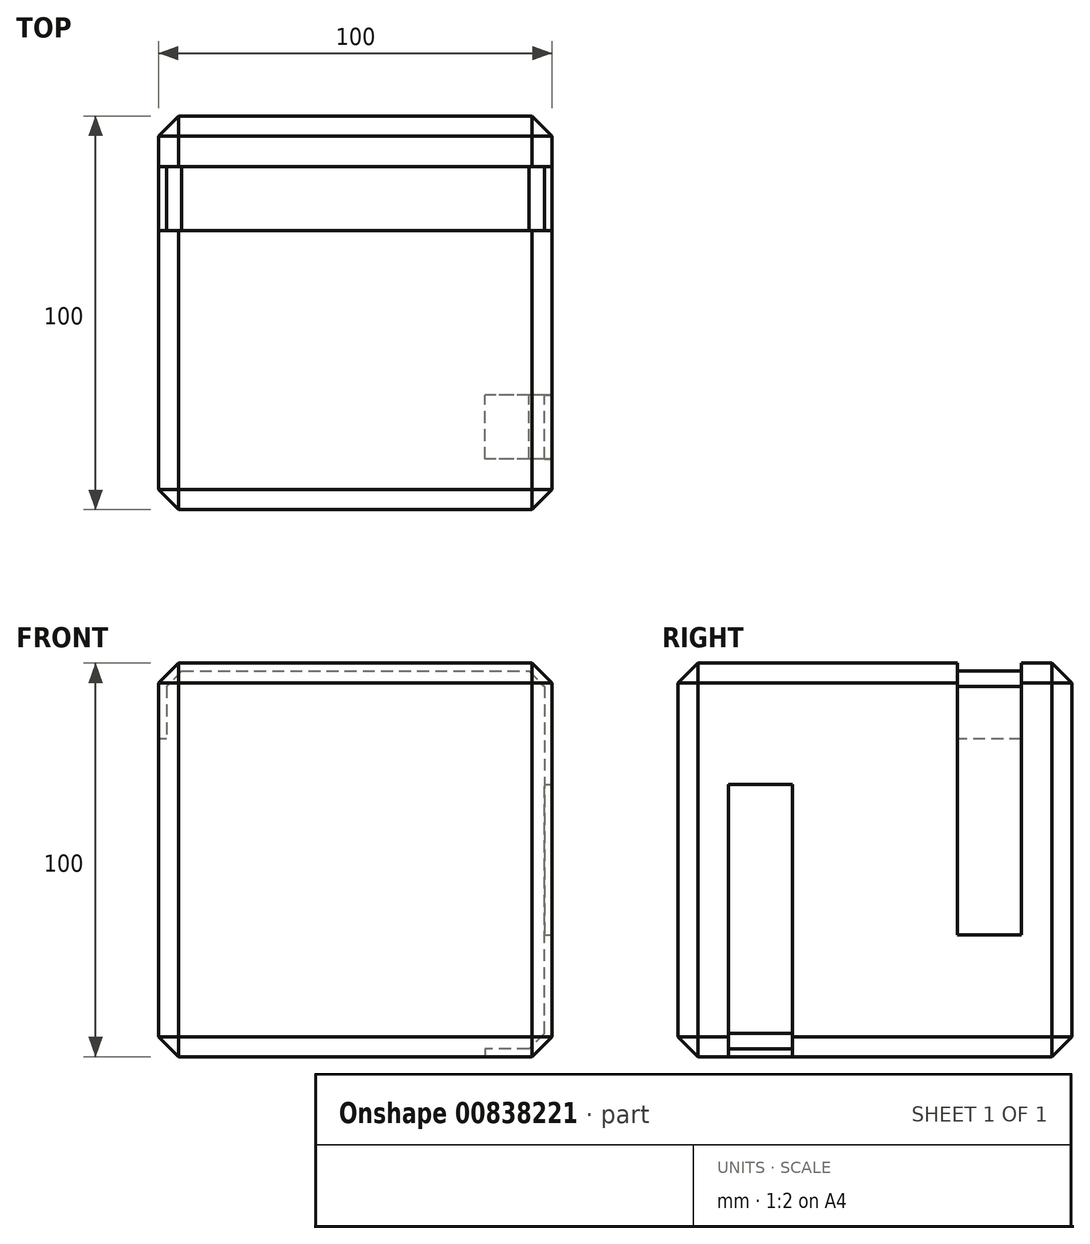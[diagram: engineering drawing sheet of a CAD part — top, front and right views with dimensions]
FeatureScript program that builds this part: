
annotation { "Feature Type Name" : "Feature", "Feature Type Description" : "" }
export const myFeature = defineFeature(function(context is Context, id is Id, definition is map)
    precondition{}
    {
        {
            var Q0;
            Q0=qCreatedBy(makeId("Top.planeOp"),FACE);
            var sketch = newSketch(context, id + "F0", { "sketchPlane" : qUnion([Q0])});
            skLineSegment(sketch, "E0.bottom", {"start": v(-47.47, 48.15) * mm, "end": v(52.53, 48.15) * mm});
            skLineSegment(sketch, "E0.top", {"start": v(-47.47, -51.85) * mm, "end": v(52.53, -51.85) * mm});
            skLineSegment(sketch, "E0.left", {"start": v(-47.47, 48.15) * mm, "end": v(-47.47, -51.85) * mm});
            skLineSegment(sketch, "E0.right", {"start": v(52.53, 48.15) * mm, "end": v(52.53, -51.85) * mm});
            skSolve(sketch);
        }
        {
            var Q0;
            Q0=makeQuery(id+"F0.imprint","IMPRINT",FACE,{"disambiguationData":[TD([[makeQuery(id+"F0.imprint","IMPRINT",EDGE,{"derivedFrom":sQuery(id+"F0.wireOp",EDGE,"E0.bottom")}),-1.0]])]});
            extrude(context, id + "F1", {"entities" : qUnion([Q0]), "depth" : 100 * mm, "offsetDistance" : 25.4 * mm});
        }
        {
            var Q0;
            Q0=makeQuery(id+"F1.opExtrude","CAP_EDGE",EDGE,{"disambiguationData":[OSD([sQuery(id+"F0.wireOp",EDGE,"E0.top")])],"isStart":false});
            var Q1;
            Q1=makeQuery(id+"F1.opExtrude","CAP_EDGE",EDGE,{"disambiguationData":[OSD([sQuery(id+"F0.wireOp",EDGE,"E0.left")])],"isStart":false});
            var Q2;
            Q2=makeQuery(id+"F1.opExtrude","SWEPT_EDGE",EDGE,{"disambiguationData":[OSD([sQuery(id+"F0.wireOp",EDGE,"E0.top"),sQuery(id+"F0.wireOp",EDGE,"E0.left")])]});
            var Q3;
            Q3=makeQuery(id+"F1.opExtrude","SWEPT_EDGE",EDGE,{"disambiguationData":[OSD([sQuery(id+"F0.wireOp",EDGE,"E0.top"),sQuery(id+"F0.wireOp",EDGE,"E0.right")])]});
            var Q4;
            Q4=makeQuery(id+"F1.opExtrude","CAP_EDGE",EDGE,{"disambiguationData":[OSD([sQuery(id+"F0.wireOp",EDGE,"E0.top")])],"isStart":true});
            var Q5;
            Q5=makeQuery(id+"F1.opExtrude","CAP_EDGE",EDGE,{"disambiguationData":[OSD([sQuery(id+"F0.wireOp",EDGE,"E0.right")])],"isStart":true});
            var Q6;
            Q6=makeQuery(id+"F1.opExtrude","CAP_EDGE",EDGE,{"disambiguationData":[OSD([sQuery(id+"F0.wireOp",EDGE,"E0.bottom")])],"isStart":true});
            var Q7;
            Q7=makeQuery(id+"F1.opExtrude","SWEPT_EDGE",EDGE,{"disambiguationData":[OSD([sQuery(id+"F0.wireOp",EDGE,"E0.bottom"),sQuery(id+"F0.wireOp",EDGE,"E0.right")])]});
            var Q8;
            Q8=makeQuery(id+"F1.opExtrude","SWEPT_EDGE",EDGE,{"disambiguationData":[OSD([sQuery(id+"F0.wireOp",EDGE,"E0.bottom"),sQuery(id+"F0.wireOp",EDGE,"E0.left")])]});
            var Q9;
            Q9=makeQuery(id+"F1.opExtrude","CAP_EDGE",EDGE,{"disambiguationData":[OSD([sQuery(id+"F0.wireOp",EDGE,"E0.left")])],"isStart":true});
            var Q10;
            Q10=makeQuery(id+"F1.opExtrude","CAP_EDGE",EDGE,{"disambiguationData":[OSD([sQuery(id+"F0.wireOp",EDGE,"E0.bottom")])],"isStart":false});
            var Q11;
            Q11=makeQuery(id+"F1.opExtrude","CAP_EDGE",EDGE,{"disambiguationData":[OSD([sQuery(id+"F0.wireOp",EDGE,"E0.right")])],"isStart":false});
            chamfer(context, id + "F2", {"entities" : qUnion([Q0, Q1, Q2, Q3, Q4, Q5, Q6, Q7, Q8, Q9, Q10, Q11]), "width" : 5.08 * mm, "tangentPropagation" : true});
        }
        {
            var Q0;
            Q0=makeQuery(id+"F1.opExtrude","CAP_FACE",FACE,{"disambiguationData":[OSD([sQuery(id+"F0.wireOp",EDGE,"E0.bottom"),sQuery(id+"F0.wireOp",EDGE,"E0.top"),sQuery(id+"F0.wireOp",EDGE,"E0.left"),sQuery(id+"F0.wireOp",EDGE,"E0.right")])],"isStart":false});
            var sketch = newSketch(context, id + "F3", { "sketchPlane" : qUnion([Q0])});
            skLineSegment(sketch, "E1.bottom", {"start": v(-42.4, 35.32) * mm, "end": v(47.45, 35.32) * mm});
            skLineSegment(sketch, "E1.top", {"start": v(-42.4, 19.07) * mm, "end": v(47.45, 19.07) * mm});
            skLineSegment(sketch, "E1.left", {"start": v(-42.4, 35.32) * mm, "end": v(-42.4, 19.07) * mm});
            skLineSegment(sketch, "E1.right", {"start": v(47.45, 35.32) * mm, "end": v(47.45, 19.07) * mm});
            skSolve(sketch);
        }
        {
            var Q0;
            Q0=makeQuery(id+"F3.imprint","IMPRINT",FACE,{"disambiguationData":[TD([[makeQuery(id+"F3.imprint","IMPRINT",EDGE,{"derivedFrom":sQuery(id+"F3.wireOp",EDGE,"E1.bottom")}),-1.0]])]});
            extrude(context, id + "F4", {"entities" : qUnion([Q0]), "operationType" : NewBodyOperationType.REMOVE, "oppositeDirection" : true, "depth" : 2 * mm, "offsetDistance" : 25.4 * mm});
        }
        {
            var Q0;
            {var subQ0=sQuery(id+"F0.wireOp",EDGE,"E0.left");Q0=makeQuery(id+"F2.opChamfer","BLEND_FACE",FACE,{"disambiguationData":[OSD([subQ0]),TDD([makeQuery(id+"F1.opExtrude","CAP_EDGE",EDGE,{"disambiguationData":[OSD([subQ0])],"isStart":false})])]});}
            var sketch = newSketch(context, id + "F5", { "sketchPlane" : qUnion([Q0])});
            skLineSegment(sketch, "E2.bottom", {"start": v(-35.32, 40.73) * mm, "end": v(-19.07, 40.73) * mm});
            skLineSegment(sketch, "E2.top", {"start": v(-35.32, 33.55) * mm, "end": v(-19.07, 33.55) * mm});
            skLineSegment(sketch, "E2.left", {"start": v(-35.32, 40.73) * mm, "end": v(-35.32, 33.55) * mm});
            skLineSegment(sketch, "E2.right", {"start": v(-19.07, 40.73) * mm, "end": v(-19.07, 33.55) * mm});
            skSolve(sketch);
        }
        {
            var Q0;
            Q0=makeQuery(id+"F5.imprint","IMPRINT",FACE,{"disambiguationData":[TD([[makeQuery(id+"F5.imprint","IMPRINT",EDGE,{"derivedFrom":sQuery(id+"F5.wireOp",EDGE,"E2.top")}),-1.0]])]});
            extrude(context, id + "F6", {"entities" : qUnion([Q0]), "operationType" : NewBodyOperationType.REMOVE, "oppositeDirection" : true, "depth" : 2 * mm, "offsetDistance" : 25.4 * mm});
        }
        {
            var Q0;
            Q0=makeQuery(id+"F1.opExtrude","SWEPT_FACE",FACE,{"disambiguationData":[OSD([sQuery(id+"F0.wireOp",EDGE,"E0.left")])]});
            var sketch = newSketch(context, id + "F7", { "sketchPlane" : qUnion([Q0])});
            skLineSegment(sketch, "E3.bottom", {"start": v(-35.32, 94.92) * mm, "end": v(-19.07, 94.92) * mm});
            skLineSegment(sketch, "E3.top", {"start": v(-35.32, 80.69) * mm, "end": v(-19.07, 80.69) * mm});
            skLineSegment(sketch, "E3.left", {"start": v(-35.32, 94.92) * mm, "end": v(-35.32, 80.69) * mm});
            skLineSegment(sketch, "E3.right", {"start": v(-19.07, 94.92) * mm, "end": v(-19.07, 80.69) * mm});
            skSolve(sketch);
        }
        {
            var Q0;
            Q0=makeQuery(id+"F7.imprint","IMPRINT",FACE,{"disambiguationData":[TD([[makeQuery(id+"F7.imprint","IMPRINT",EDGE,{"derivedFrom":sQuery(id+"F7.wireOp",EDGE,"E3.bottom")}),1.0]])]});
            extrude(context, id + "F8", {"entities" : qUnion([Q0]), "operationType" : NewBodyOperationType.REMOVE, "oppositeDirection" : true, "depth" : 2 * mm, "offsetDistance" : 25.4 * mm});
        }
        {
            var Q0;
            {var subQ0=sQuery(id+"F0.wireOp",EDGE,"E0.right");Q0=makeQuery(id+"F2.opChamfer","BLEND_FACE",FACE,{"disambiguationData":[OSD([subQ0]),TDD([makeQuery(id+"F1.opExtrude","CAP_EDGE",EDGE,{"disambiguationData":[OSD([subQ0])],"isStart":false})])]});}
            var sketch = newSketch(context, id + "F9", { "sketchPlane" : qUnion([Q0])});
            skLineSegment(sketch, "E4.bottom", {"start": v(35.32, 37.16) * mm, "end": v(19.07, 37.16) * mm});
            skLineSegment(sketch, "E4.top", {"start": v(35.32, 29.98) * mm, "end": v(19.07, 29.98) * mm});
            skLineSegment(sketch, "E4.left", {"start": v(35.32, 37.16) * mm, "end": v(35.32, 29.98) * mm});
            skLineSegment(sketch, "E4.right", {"start": v(19.07, 37.16) * mm, "end": v(19.07, 29.98) * mm});
            skSolve(sketch);
        }
        {
            var Q0;
            Q0=makeQuery(id+"F9.imprint","IMPRINT",FACE,{"disambiguationData":[TD([[makeQuery(id+"F9.imprint","IMPRINT",EDGE,{"derivedFrom":sQuery(id+"F9.wireOp",EDGE,"E4.bottom")}),-1.0]])]});
            extrude(context, id + "F10", {"entities" : qUnion([Q0]), "operationType" : NewBodyOperationType.REMOVE, "oppositeDirection" : true, "depth" : 2 * mm, "offsetDistance" : 25.4 * mm});
        }
        {
            var Q0;
            Q0=makeQuery(id+"F1.opExtrude","SWEPT_FACE",FACE,{"disambiguationData":[OSD([sQuery(id+"F0.wireOp",EDGE,"E0.right")])]});
            var sketch = newSketch(context, id + "F11", { "sketchPlane" : qUnion([Q0])});
            skLineSegment(sketch, "E5.bottom", {"start": v(35.32, 94.92) * mm, "end": v(19.07, 94.92) * mm});
            skLineSegment(sketch, "E5.top", {"start": v(35.32, 30.89) * mm, "end": v(19.07, 30.89) * mm});
            skLineSegment(sketch, "E5.left", {"start": v(35.32, 94.92) * mm, "end": v(35.32, 30.89) * mm});
            skLineSegment(sketch, "E5.right", {"start": v(19.07, 94.92) * mm, "end": v(19.07, 30.89) * mm});
            skSolve(sketch);
        }
        {
            var Q0;
            Q0=makeQuery(id+"F11.imprint","IMPRINT",FACE,{"disambiguationData":[TD([[makeQuery(id+"F11.imprint","IMPRINT",EDGE,{"derivedFrom":sQuery(id+"F11.wireOp",EDGE,"E5.bottom")}),1.0]])]});
            extrude(context, id + "F12", {"entities" : qUnion([Q0]), "operationType" : NewBodyOperationType.REMOVE, "oppositeDirection" : true, "depth" : 2 * mm, "offsetDistance" : 25.4 * mm});
        }
        {
            var Q0;
            Q0=makeQuery(id+"F1.opExtrude","SWEPT_FACE",FACE,{"disambiguationData":[OSD([sQuery(id+"F0.wireOp",EDGE,"E0.right")])]});
            var sketch = newSketch(context, id + "F13", { "sketchPlane" : qUnion([Q0])});
            skLineSegment(sketch, "E6", {"start": v(-46.77, 5.08) * mm, "end": v(-39.02, 5.08) * mm});
            skLineSegment(sketch, "E7.bottom", {"start": v(-39.02, 5.08) * mm, "end": v(-22.76, 5.08) * mm});
            skLineSegment(sketch, "E7.top", {"start": v(-39.02, 69.11) * mm, "end": v(-22.76, 69.11) * mm});
            skLineSegment(sketch, "E7.left", {"start": v(-39.02, 5.08) * mm, "end": v(-39.02, 69.11) * mm});
            skLineSegment(sketch, "E7.right", {"start": v(-22.76, 5.08) * mm, "end": v(-22.76, 69.11) * mm});
            skSolve(sketch);
        }
        {
            var Q0;
            Q0=makeQuery(id+"F13.imprint","IMPRINT",FACE,{"disambiguationData":[TD([[makeQuery(id+"F13.imprint","IMPRINT",EDGE,{"derivedFrom":sQuery(id+"F13.wireOp",EDGE,"E7.bottom")}),1.0]])]});
            extrude(context, id + "F14", {"entities" : qUnion([Q0]), "operationType" : NewBodyOperationType.REMOVE, "oppositeDirection" : true, "depth" : 2 * mm, "offsetDistance" : 25.4 * mm});
        }
        {
            var Q0;
            {var subQ0=sQuery(id+"F0.wireOp",EDGE,"E0.right");Q0=makeQuery(id+"F2.opChamfer","BLEND_FACE",FACE,{"disambiguationData":[OSD([subQ0]),TDD([makeQuery(id+"F1.opExtrude","CAP_EDGE",EDGE,{"disambiguationData":[OSD([subQ0])],"isStart":true})])]});}
            var sketch = newSketch(context, id + "F15", { "sketchPlane" : qUnion([Q0])});
            skLineSegment(sketch, "E8.bottom", {"start": v(-39.02, 40.73) * mm, "end": v(-22.76, 40.73) * mm});
            skLineSegment(sketch, "E8.top", {"start": v(-39.02, 33.55) * mm, "end": v(-22.76, 33.55) * mm});
            skLineSegment(sketch, "E8.left", {"start": v(-39.02, 40.73) * mm, "end": v(-39.02, 33.55) * mm});
            skLineSegment(sketch, "E8.right", {"start": v(-22.76, 40.73) * mm, "end": v(-22.76, 33.55) * mm});
            skSolve(sketch);
        }
        {
            var Q0;
            Q0=makeQuery(id+"F15.imprint","IMPRINT",FACE,{"disambiguationData":[TD([[makeQuery(id+"F15.imprint","IMPRINT",EDGE,{"derivedFrom":sQuery(id+"F15.wireOp",EDGE,"E8.bottom")}),-1.0]])]});
            extrude(context, id + "F16", {"entities" : qUnion([Q0]), "operationType" : NewBodyOperationType.REMOVE, "oppositeDirection" : true, "depth" : 2 * mm, "offsetDistance" : 25.4 * mm});
        }
        {
            var Q0;
            Q0=makeQuery(id+"F1.opExtrude","CAP_FACE",FACE,{"disambiguationData":[OSD([sQuery(id+"F0.wireOp",EDGE,"E0.bottom"),sQuery(id+"F0.wireOp",EDGE,"E0.top"),sQuery(id+"F0.wireOp",EDGE,"E0.left"),sQuery(id+"F0.wireOp",EDGE,"E0.right")])],"isStart":true});
            var sketch = newSketch(context, id + "F17", { "sketchPlane" : qUnion([Q0])});
            skLineSegment(sketch, "E9.bottom", {"start": v(47.45, 39.02) * mm, "end": v(35.5, 39.02) * mm});
            skLineSegment(sketch, "E9.top", {"start": v(47.45, 22.76) * mm, "end": v(35.5, 22.76) * mm});
            skLineSegment(sketch, "E9.left", {"start": v(47.45, 39.02) * mm, "end": v(47.45, 22.76) * mm});
            skLineSegment(sketch, "E9.right", {"start": v(35.5, 39.02) * mm, "end": v(35.5, 22.76) * mm});
            skSolve(sketch);
        }
        {
            var Q0;
            Q0 = qSketchRegion(id + "F17", true);
            extrude(context, id + "F18", {"entities" : qUnion([Q0]), "operationType" : NewBodyOperationType.REMOVE, "oppositeDirection" : true, "depth" : 2 * mm, "offsetDistance" : 25.4 * mm});
        }
    });
